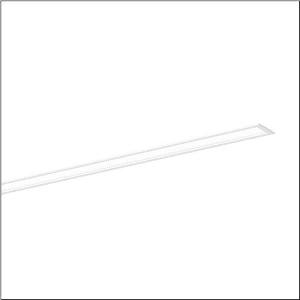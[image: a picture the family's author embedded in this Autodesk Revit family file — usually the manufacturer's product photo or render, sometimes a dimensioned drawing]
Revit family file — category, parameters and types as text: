
# Revit family: silica_21_51mx13dj32wb
name_source: partatom
category: Lighting Fixtures
units: mm (PartAtom-declared; Revit-internal decimal feet)

## family parameters
Cut with Voids When Loaded = No
Host = Face
Light Source = No
Part Type = Normal
Room Calculation Point = No
Round Connector Dimension = Use Diameter
Shared = No

## types (1)
- --- (1 x LED, 2460 lm, 19.3 W, 3000K)
    Apparent Load = 19 VA
    CIE Flux Codes = 78 96 99 100 100
    Color Rendering = 80
    Color Temperature = 3000K
    Default Elevation = 1800 mm
    Description = Silica 21, office luminaire, primary optical cover: prismatic diffuser, of PMMA, CAT 2 (L<= 3000cd/m²), light emission: direct distribution, primary light characteristic: symmetric, installation type: recessed, LED, rated luminous flux: 2.460lm, luminous efficacy: 128lm/W, light colour: 830, colour temperature: 3000K, control gear: DALI 2, with terminal, 3+2-pole, max. 2.5mm², mains connection: 220..240V, AC, 50/60Hz, rated input power: 19.3W, luminaire housing, of aluminium, traffic white (RAL 9016), length: 928mm, width: 79mm, height: 53mm, protection rating (complete): IP20, insulation class (complete): insulation class I (protective earthing), certification: CE, permissible operating ambient temperature: 0..+35°C, standard: EN 50419, packaging unit: 1 piece
    Height = 0 mm  [stored 0 ft]
    Lamp = 1 x LED
    Lamp Light Flux = 2460 lm
    Lamp Power = 19.3 W
    Lamp count = 1
    Length = 927 mm
    Luminous efficacy = 127 lm/W
    Manufacturer = Siteco
    ModVariant = No
    Model = 51MX13DJ32WB
    Mounting Place = Ceiling
    Mounting Type = Recessed
    Number of Poles = 1
    OnlyDefault = Yes
    Power Factor = 1
    Product Name = Silica 21
    Product group = office luminaire | ceiling recessed
    ProductGroupID = 400
    Protection Class = Protection class I
    Protection Degree = IP 20
    RLX_Detail_Level = 1
    RLX_Emergency_Light_Flux = 0 lm
    RLX_Emergency_Type = 0
    RLX_Emergency_Type_DB = No
    RlxData = <blob elided: 14369 chars, md5=6cd503dc>
    Socket = socket
    Standby Power = 0 W
    System Light Flux = 2460 lm
    System Power = 19 W
    Type Comments = factory setting: luminous flux: 100 % | dim-lin: 254 | 171 mA
    Type Image = l_1335881.jpg
    URL = http://relux.com
    VarID = @adj_031127
    Voltage = 0 V
    Weight = 0.00 kg
    Width = 79 mm

note: [stored X ft] marks values corroborated as IEEE doubles in the binary element streams (Revit-internal decimal feet)

## geometry (parser evidence)
native form markers: Sweep x12
no freeform markers — native parametric forms only
